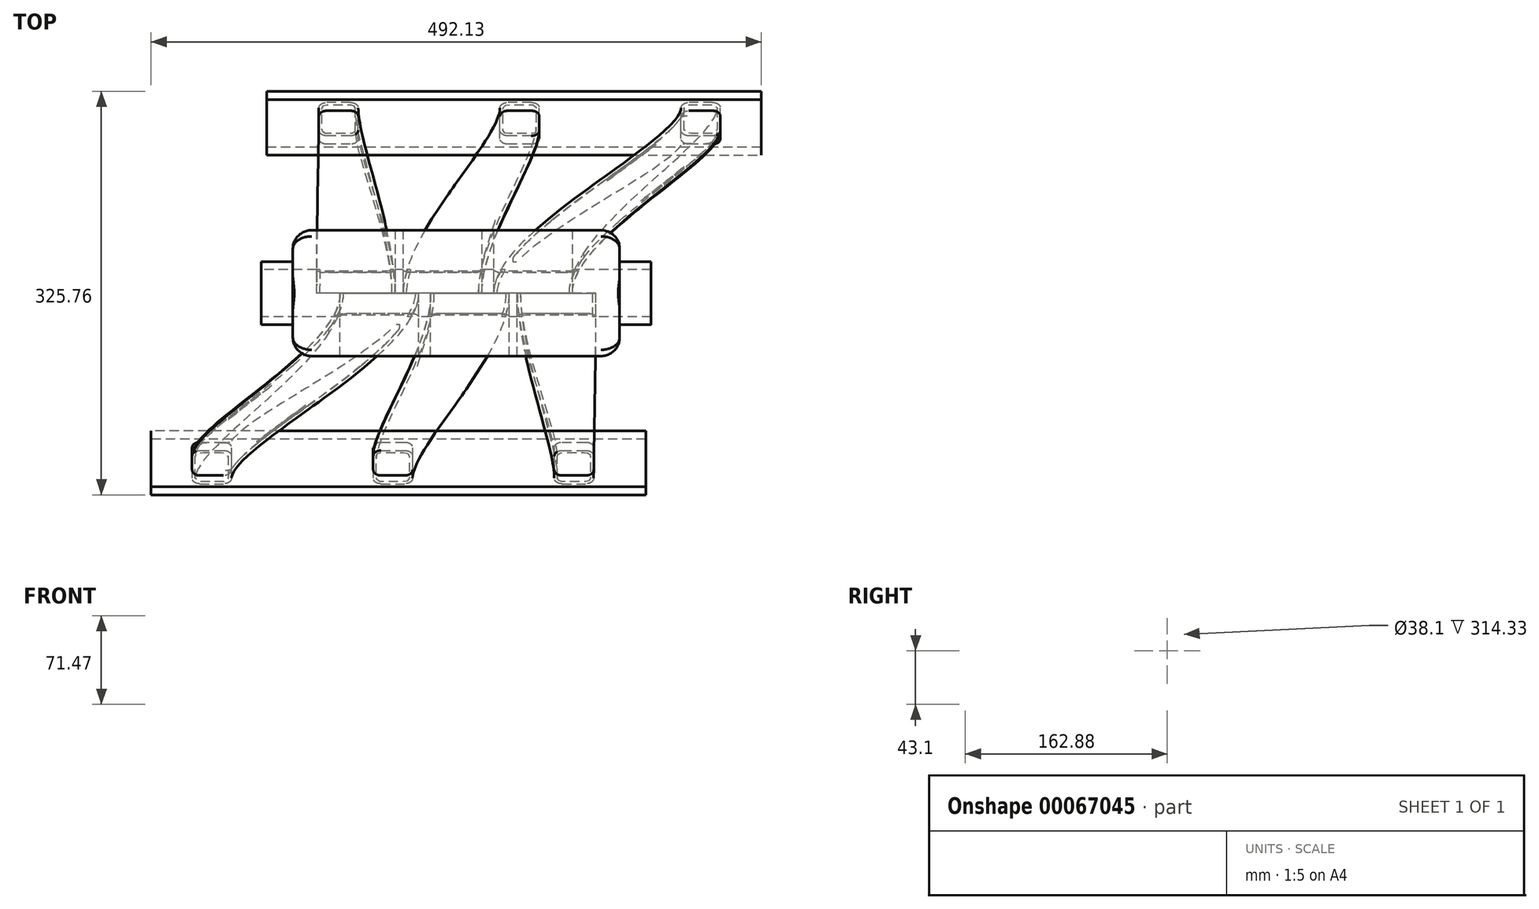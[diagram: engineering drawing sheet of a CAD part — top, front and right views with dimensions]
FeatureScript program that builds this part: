
annotation { "Feature Type Name" : "Feature", "Feature Type Description" : "" }
export const myFeature = defineFeature(function(context is Context, id is Id, definition is map)
    precondition{}
    {
        {
            var Q0;
            Q0=qCreatedBy(makeId("Front.planeOp"),FACE);
            var sketch = newSketch(context, id + "F0", { "sketchPlane" : qUnion([Q0])});
            skLineSegment(sketch, "E0.bottom", {"start": v(-123.83, 301.55) * mm, "end": v(139.7, 301.55) * mm});
            skLineSegment(sketch, "E0.top", {"start": v(-123.83, 230.08) * mm, "end": v(139.7, 230.08) * mm});
            skLineSegment(sketch, "E0.left", {"start": v(-123.83, 301.55) * mm, "end": v(-123.83, 230.08) * mm});
            skLineSegment(sketch, "E0.right", {"start": v(139.7, 301.55) * mm, "end": v(139.7, 230.08) * mm});
            skLineSegment(sketch, "E1.bottom", {"start": v(63.5, 282.5) * mm, "end": v(114.3, 282.5) * mm});
            skLineSegment(sketch, "E1.top", {"start": v(63.5, 244.4) * mm, "end": v(114.3, 244.4) * mm});
            skLineSegment(sketch, "E1.left", {"start": v(57.15, 276.15) * mm, "end": v(57.15, 250.75) * mm});
            skLineSegment(sketch, "E1.right", {"start": v(120.65, 276.15) * mm, "end": v(120.65, 250.75) * mm});
            skPoint(sketch, "E2.visualSharp", {"position": v(57.15, 282.5) * mm});
            skArc(sketch, "E2.filletArc", {"start": v(63.5, 282.5) * mm, "mid": v(59, 280.64) * mm, "end": v(57.15, 276.15) * mm});
            skPoint(sketch, "E3.visualSharp", {"position": v(120.65, 282.5) * mm});
            skArc(sketch, "E3.filletArc", {"start": v(120.65, 276.15) * mm, "mid": v(118.8, 280.64) * mm, "end": v(114.3, 282.5) * mm});
            skPoint(sketch, "E4.visualSharp", {"position": v(120.65, 244.4) * mm});
            skArc(sketch, "E4.filletArc", {"start": v(114.3, 244.4) * mm, "mid": v(118.8, 246.26) * mm, "end": v(120.65, 250.75) * mm});
            skPoint(sketch, "E5.visualSharp", {"position": v(57.15, 244.4) * mm});
            skArc(sketch, "E5.filletArc", {"start": v(57.15, 250.75) * mm, "mid": v(59, 246.26) * mm, "end": v(63.5, 244.4) * mm});
            skLineSegment(sketch, "E6.1.0.0", {"start": v(-6.35, 282.5) * mm, "end": v(44.45, 282.5) * mm});
            skArc(sketch, "E6.1.0.1", {"start": v(-6.35, 282.5) * mm, "mid": v(-10.84, 280.64) * mm, "end": v(-12.7, 276.15) * mm});
            skLineSegment(sketch, "E6.1.0.2", {"start": v(-12.7, 276.15) * mm, "end": v(-12.7, 250.75) * mm});
            skArc(sketch, "E6.1.0.3", {"start": v(-12.7, 250.75) * mm, "mid": v(-10.84, 246.26) * mm, "end": v(-6.35, 244.4) * mm});
            skLineSegment(sketch, "E6.1.0.4", {"start": v(-6.35, 244.4) * mm, "end": v(44.45, 244.4) * mm});
            skArc(sketch, "E6.1.0.5", {"start": v(44.45, 244.4) * mm, "mid": v(48.94, 246.26) * mm, "end": v(50.8, 250.75) * mm});
            skLineSegment(sketch, "E6.1.0.6", {"start": v(50.8, 276.15) * mm, "end": v(50.8, 250.75) * mm});
            skArc(sketch, "E6.1.0.7", {"start": v(50.8, 276.15) * mm, "mid": v(48.94, 280.64) * mm, "end": v(44.45, 282.5) * mm});
            skLineSegment(sketch, "E6.direction1", {"start": v(63.5, 282.5) * mm, "end": v(-6.35, 282.5) * mm, "construction": true});
            skLineSegment(sketch, "E7.1.0.0", {"start": v(-85.73, 276.15) * mm, "end": v(-85.73, 250.75) * mm});
            skLineSegment(sketch, "E7.1.0.1", {"start": v(-79.38, 282.5) * mm, "end": v(-28.58, 282.5) * mm});
            skArc(sketch, "E7.1.0.2", {"start": v(-79.38, 282.5) * mm, "mid": v(-83.87, 280.64) * mm, "end": v(-85.73, 276.15) * mm});
            skArc(sketch, "E7.1.0.3", {"start": v(-85.73, 250.75) * mm, "mid": v(-83.87, 246.26) * mm, "end": v(-79.38, 244.4) * mm});
            skLineSegment(sketch, "E7.1.0.4", {"start": v(-79.38, 244.4) * mm, "end": v(-28.58, 244.4) * mm});
            skArc(sketch, "E7.1.0.5", {"start": v(-28.58, 244.4) * mm, "mid": v(-24.09, 246.26) * mm, "end": v(-22.23, 250.75) * mm});
            skLineSegment(sketch, "E7.1.0.6", {"start": v(-22.23, 276.15) * mm, "end": v(-22.23, 250.75) * mm});
            skArc(sketch, "E7.1.0.7", {"start": v(-22.23, 276.15) * mm, "mid": v(-24.09, 280.64) * mm, "end": v(-28.58, 282.5) * mm});
            skLineSegment(sketch, "E7.direction1", {"start": v(57.15, 250.75) * mm, "end": v(-85.73, 250.75) * mm, "construction": true});
            skSolve(sketch);
        }
        {
            var Q0;
            Q0=qCreatedBy(makeId("Front.planeOp"),FACE);
            var Q1;
            Q1=qCreatedBy(makeId("Top.planeOp"),FACE);
            cPlane(context, id + "F1", {"entities" : qUnion([Q0, Q1]), "cplaneType" : CPlaneType.MID_PLANE, "offset" : 152.4 * mm, "width" : 152.4 * mm, "height" : 152.4 * mm});
        }
        {
            var Q0;
            Q0=qCreatedBy(id+"F1.planeOp",FACE);
            cPlane(context, id + "F2", {"entities" : qUnion([Q0]), "cplaneType" : CPlaneType.OFFSET, "offset" : 82.55 * mm, "oppositeDirection" : true, "width" : 152.4 * mm, "height" : 152.4 * mm});
        }
        {
            var Q0;
            Q0=qCreatedBy(id+"F2.planeOp",FACE);
            var sketch = newSketch(context, id + "F3", { "sketchPlane" : qUnion([Q0])});
            skLineSegment(sketch, "E8.bottom", {"start": v(160.76, 312.9) * mm, "end": v(-238.13, 312.9) * mm});
            skLineSegment(sketch, "E8.top", {"start": v(160.76, 249.4) * mm, "end": v(-238.13, 249.4) * mm});
            skLineSegment(sketch, "E8.left", {"start": v(160.76, 312.9) * mm, "end": v(160.76, 249.4) * mm});
            skLineSegment(sketch, "E8.right", {"start": v(-238.13, 312.9) * mm, "end": v(-238.13, 249.4) * mm});
            skLineSegment(sketch, "E9.rect.bottom", {"start": v(-198.76, 262.1) * mm, "end": v(-179.71, 262.1) * mm});
            skLineSegment(sketch, "E9.rect.top", {"start": v(-198.76, 300.2) * mm, "end": v(-179.71, 300.2) * mm});
            skLineSegment(sketch, "E9.rect.left", {"start": v(-205.11, 268.45) * mm, "end": v(-205.11, 293.85) * mm});
            skLineSegment(sketch, "E9.rect.right", {"start": v(-173.36, 268.45) * mm, "end": v(-173.36, 293.85) * mm});
            skPoint(sketch, "E9.rect.middle", {"position": v(-189.24, 281.15) * mm});
            skLineSegment(sketch, "E10", {"start": v(-238.13, 281.15) * mm, "end": v(160.76, 281.15) * mm, "construction": true});
            skPoint(sketch, "E11.visualSharp", {"position": v(-173.36, 300.2) * mm});
            skArc(sketch, "E11.filletArc", {"start": v(-173.36, 293.85) * mm, "mid": v(-175.22, 298.34) * mm, "end": v(-179.71, 300.2) * mm});
            skPoint(sketch, "E12.visualSharp", {"position": v(-205.11, 300.2) * mm});
            skArc(sketch, "E12.filletArc", {"start": v(-198.76, 300.2) * mm, "mid": v(-203.25, 298.34) * mm, "end": v(-205.11, 293.85) * mm});
            skPoint(sketch, "E13.visualSharp", {"position": v(-173.36, 262.1) * mm});
            skArc(sketch, "E13.filletArc", {"start": v(-179.71, 262.1) * mm, "mid": v(-175.22, 263.96) * mm, "end": v(-173.36, 268.45) * mm});
            skPoint(sketch, "E14.visualSharp", {"position": v(-205.11, 262.1) * mm});
            skArc(sketch, "E14.filletArc", {"start": v(-205.11, 268.45) * mm, "mid": v(-203.25, 263.96) * mm, "end": v(-198.76, 262.1) * mm});
            skLineSegment(sketch, "E15.1.0.0", {"start": v(-52.71, 262.1) * mm, "end": v(-33.66, 262.1) * mm});
            skArc(sketch, "E15.1.0.1", {"start": v(-33.66, 262.1) * mm, "mid": v(-29.17, 263.96) * mm, "end": v(-27.31, 268.45) * mm});
            skLineSegment(sketch, "E15.1.0.2", {"start": v(-27.31, 268.45) * mm, "end": v(-27.31, 293.85) * mm});
            skArc(sketch, "E15.1.0.3", {"start": v(-27.31, 293.85) * mm, "mid": v(-29.17, 298.34) * mm, "end": v(-33.66, 300.2) * mm});
            skLineSegment(sketch, "E15.1.0.4", {"start": v(-52.71, 300.2) * mm, "end": v(-33.66, 300.2) * mm});
            skArc(sketch, "E15.1.0.5", {"start": v(-52.71, 300.2) * mm, "mid": v(-57.2, 298.34) * mm, "end": v(-59.06, 293.85) * mm});
            skLineSegment(sketch, "E15.1.0.6", {"start": v(-59.06, 268.45) * mm, "end": v(-59.06, 293.85) * mm});
            skArc(sketch, "E15.1.0.7", {"start": v(-59.06, 268.45) * mm, "mid": v(-57.2, 263.96) * mm, "end": v(-52.71, 262.1) * mm});
            skLineSegment(sketch, "E15.2.0.0", {"start": v(93.34, 262.1) * mm, "end": v(112.39, 262.1) * mm});
            skArc(sketch, "E15.2.0.1", {"start": v(112.39, 262.1) * mm, "mid": v(116.88, 263.96) * mm, "end": v(118.74, 268.45) * mm});
            skLineSegment(sketch, "E15.2.0.2", {"start": v(118.74, 268.45) * mm, "end": v(118.74, 293.85) * mm});
            skArc(sketch, "E15.2.0.3", {"start": v(118.74, 293.85) * mm, "mid": v(116.88, 298.34) * mm, "end": v(112.39, 300.2) * mm});
            skLineSegment(sketch, "E15.2.0.4", {"start": v(93.34, 300.2) * mm, "end": v(112.39, 300.2) * mm});
            skArc(sketch, "E15.2.0.5", {"start": v(93.34, 300.2) * mm, "mid": v(88.85, 298.34) * mm, "end": v(86.99, 293.85) * mm});
            skLineSegment(sketch, "E15.2.0.6", {"start": v(86.99, 268.45) * mm, "end": v(86.99, 293.85) * mm});
            skArc(sketch, "E15.2.0.7", {"start": v(86.99, 268.45) * mm, "mid": v(88.85, 263.96) * mm, "end": v(93.34, 262.1) * mm});
            skLineSegment(sketch, "E15.direction1", {"start": v(-198.76, 262.1) * mm, "end": v(-52.71, 262.1) * mm, "construction": true});
            skSolve(sketch);
        }
        {
            var Q0;
            Q0=makeQuery(id+"F0.imprint","IMPRINT",FACE,{"disambiguationData":[TD([[makeQuery(id+"F0.imprint","IMPRINT",EDGE,{"derivedFrom":sQuery(id+"F0.wireOp",EDGE,"E7.1.0.0")}),1.0]])]});
            var Q1;
            Q1=makeQuery(id+"F3.imprint","IMPRINT",FACE,{"disambiguationData":[TD([[makeQuery(id+"F3.imprint","IMPRINT",EDGE,{"derivedFrom":sQuery(id+"F3.wireOp",EDGE,"E9.rect.bottom")}),1.0]])]});
            loft(context, id + "F4", {"startCondition" : LoftEndDerivativeType.NORMAL_TO_PROFILE, "startMagnitude" : 1, "endCondition" : LoftEndDerivativeType.NORMAL_TO_PROFILE, "endMagnitude" : 1, "sheetProfilesArray" : [{ "sheetProfileEntities" : qUnion([Q0]) }, { "sheetProfileEntities" : qUnion([Q1]) }]});
        }
        {
            var Q0;
            Q0=makeQuery(id+"F0.imprint","IMPRINT",FACE,{"disambiguationData":[TD([[makeQuery(id+"F0.imprint","IMPRINT",EDGE,{"derivedFrom":sQuery(id+"F0.wireOp",EDGE,"E6.1.0.0")}),-1.0]])]});
            var Q1;
            Q1=makeQuery(id+"F3.imprint","IMPRINT",FACE,{"disambiguationData":[TD([[makeQuery(id+"F3.imprint","IMPRINT",EDGE,{"derivedFrom":sQuery(id+"F3.wireOp",EDGE,"E15.1.0.0")}),1.0]])]});
            loft(context, id + "F5", {"startCondition" : LoftEndDerivativeType.NORMAL_TO_PROFILE, "startMagnitude" : 1, "endCondition" : LoftEndDerivativeType.NORMAL_TO_PROFILE, "endMagnitude" : 1, "sheetProfilesArray" : [{ "sheetProfileEntities" : qUnion([Q0]) }, { "sheetProfileEntities" : qUnion([Q1]) }]});
        }
        {
            var Q0;
            Q0=makeQuery(id+"F0.imprint","IMPRINT",FACE,{"disambiguationData":[TD([[makeQuery(id+"F0.imprint","IMPRINT",EDGE,{"derivedFrom":sQuery(id+"F0.wireOp",EDGE,"E1.bottom")}),-1.0]])]});
            var Q1;
            Q1=makeQuery(id+"F3.imprint","IMPRINT",FACE,{"disambiguationData":[TD([[makeQuery(id+"F3.imprint","IMPRINT",EDGE,{"derivedFrom":sQuery(id+"F3.wireOp",EDGE,"E15.2.0.0")}),1.0]])]});
            loft(context, id + "F6", {"startCondition" : LoftEndDerivativeType.NORMAL_TO_PROFILE, "startMagnitude" : 1, "endCondition" : LoftEndDerivativeType.NORMAL_TO_PROFILE, "endMagnitude" : 1, "sheetProfilesArray" : [{ "sheetProfileEntities" : qUnion([Q0]) }, { "sheetProfileEntities" : qUnion([Q1]) }]});
        }
        {
            var Q0;
            Q0=qSketchRegion(id+"F0",true);
            extrude(context, id + "F7", {"entities" : qUnion([Q0]), "depth" : 50.8 * mm});
        }
        {
            var Q0;
            Q0=makeQuery(id+"F4.opLoft","CAP_FACE",FACE,{"disambiguationData":[OSD([makeQuery(id+"F3.imprint","IMPRINT",FACE,{"disambiguationData":[TD([[makeQuery(id+"F3.imprint","IMPRINT",EDGE,{"derivedFrom":sQuery(id+"F3.wireOp",EDGE,"E9.rect.bottom")}),1.0]])]})])],"isStart":true});
            var Q1;
            Q1=makeQuery(id+"F4.opLoft","CAP_FACE",FACE,{"disambiguationData":[OSD([makeQuery(id+"F0.imprint","IMPRINT",FACE,{"disambiguationData":[TD([[makeQuery(id+"F0.imprint","IMPRINT",EDGE,{"derivedFrom":sQuery(id+"F0.wireOp",EDGE,"E7.1.0.0")}),1.0]])]})])],"isStart":true});
            shell(context, id + "F8", {"entities" : qUnion([Q0, Q1]), "thickness" : 2.54 * mm});
        }
        {
            var Q0;
            Q0=makeQuery(id+"F5.opLoft","CAP_FACE",FACE,{"disambiguationData":[OSD([makeQuery(id+"F0.imprint","IMPRINT",FACE,{"disambiguationData":[TD([[makeQuery(id+"F0.imprint","IMPRINT",EDGE,{"derivedFrom":sQuery(id+"F0.wireOp",EDGE,"E6.1.0.0")}),-1.0]])]})])],"isStart":true});
            var Q1;
            Q1=makeQuery(id+"F5.opLoft","CAP_FACE",FACE,{"disambiguationData":[OSD([makeQuery(id+"F3.imprint","IMPRINT",FACE,{"disambiguationData":[TD([[makeQuery(id+"F3.imprint","IMPRINT",EDGE,{"derivedFrom":sQuery(id+"F3.wireOp",EDGE,"E15.1.0.0")}),1.0]])]})])],"isStart":true});
            var Q2;
            Q2=makeQuery(id+"F5.opLoft","SWEPT_BODY",BODY,{"disambiguationData":[OSD([makeQuery(id+"F0.imprint","IMPRINT",FACE,{"disambiguationData":[TD([[makeQuery(id+"F0.imprint","IMPRINT",EDGE,{"derivedFrom":sQuery(id+"F0.wireOp",EDGE,"E6.1.0.0")}),-1.0]])]}),makeQuery(id+"F3.imprint","IMPRINT",FACE,{"disambiguationData":[TD([[makeQuery(id+"F3.imprint","IMPRINT",EDGE,{"derivedFrom":sQuery(id+"F3.wireOp",EDGE,"E15.1.0.0")}),1.0]])]})])]});
            shell(context, id + "F9", {"entities" : qUnion([Q0, Q1]), "parts" : qUnion([Q2]), "thickness" : 2.54 * mm});
        }
        {
            var Q0;
            Q0=makeQuery(id+"F6.opLoft","CAP_FACE",FACE,{"disambiguationData":[OSD([makeQuery(id+"F0.imprint","IMPRINT",FACE,{"disambiguationData":[TD([[makeQuery(id+"F0.imprint","IMPRINT",EDGE,{"derivedFrom":sQuery(id+"F0.wireOp",EDGE,"E1.bottom")}),-1.0]])]})])],"isStart":true});
            var Q1;
            Q1=makeQuery(id+"F6.opLoft","CAP_FACE",FACE,{"disambiguationData":[OSD([makeQuery(id+"F3.imprint","IMPRINT",FACE,{"disambiguationData":[TD([[makeQuery(id+"F3.imprint","IMPRINT",EDGE,{"derivedFrom":sQuery(id+"F3.wireOp",EDGE,"E15.2.0.0")}),1.0]])]})])],"isStart":true});
            shell(context, id + "F10", {"entities" : qUnion([Q0, Q1]), "thickness" : 2.54 * mm});
        }
        {
            var Q0;
            Q0=qSketchRegion(id+"F3",true);
            extrude(context, id + "F11", {"entities" : qUnion([Q0]), "oppositeDirection" : true, "depth" : 9.52 * mm});
        }
        {
            var Q0;
            Q0=makeQuery(id+"F7.opExtrude","CAP_EDGE",EDGE,{"disambiguationData":[OSD([sQuery(id+"F0.wireOp",EDGE,"E0.bottom")])],"isStart":false});
            fillet(context, id + "F12", {"entities" : qUnion([Q0]), "radius" : 5 * mm, "tangentPropagation" : true, "allowEdgeOverflow" : false});
        }
        {
            var Q0;
            Q0=makeQuery(id+"F7.opExtrude","SWEPT_EDGE",EDGE,{"disambiguationData":[OSD([sQuery(id+"F0.wireOp",EDGE,"E0.bottom"),sQuery(id+"F0.wireOp",EDGE,"E0.right")])]});
            fillet(context, id + "F13", {"entities" : qUnion([Q0]), "radius" : 15 * mm, "tangentPropagation" : true, "allowEdgeOverflow" : false});
        }
        {
            var Q0;
            Q0=makeQuery(id+"F7.opExtrude","SWEPT_EDGE",EDGE,{"disambiguationData":[OSD([sQuery(id+"F0.wireOp",EDGE,"E0.bottom"),sQuery(id+"F0.wireOp",EDGE,"E0.left")])]});
            fillet(context, id + "F14", {"entities" : qUnion([Q0]), "radius" : 15 * mm, "tangentPropagation" : true, "allowEdgeOverflow" : false});
        }
        {
            var Q0;
            Q0=makeQuery(id+"F7.opExtrude","CAP_FACE",FACE,{"disambiguationData":[OSD([sQuery(id+"F0.wireOp",EDGE,"E0.bottom"),sQuery(id+"F0.wireOp",EDGE,"E0.top"),sQuery(id+"F0.wireOp",EDGE,"E0.left"),sQuery(id+"F0.wireOp",EDGE,"E0.right"),sQuery(id+"F0.wireOp",EDGE,"E1.bottom"),sQuery(id+"F0.wireOp",EDGE,"E1.top"),sQuery(id+"F0.wireOp",EDGE,"E1.left"),sQuery(id+"F0.wireOp",EDGE,"E1.right"),sQuery(id+"F0.wireOp",EDGE,"E2.filletArc"),sQuery(id+"F0.wireOp",EDGE,"E3.filletArc"),sQuery(id+"F0.wireOp",EDGE,"E4.filletArc"),sQuery(id+"F0.wireOp",EDGE,"E5.filletArc"),sQuery(id+"F0.wireOp",EDGE,"E6.1.0.0"),sQuery(id+"F0.wireOp",EDGE,"E6.1.0.1"),sQuery(id+"F0.wireOp",EDGE,"E6.1.0.2"),sQuery(id+"F0.wireOp",EDGE,"E6.1.0.3"),sQuery(id+"F0.wireOp",EDGE,"E6.1.0.4"),sQuery(id+"F0.wireOp",EDGE,"E6.1.0.5"),sQuery(id+"F0.wireOp",EDGE,"E6.1.0.6"),sQuery(id+"F0.wireOp",EDGE,"E6.1.0.7"),sQuery(id+"F0.wireOp",EDGE,"E7.1.0.0"),sQuery(id+"F0.wireOp",EDGE,"E7.1.0.1"),sQuery(id+"F0.wireOp",EDGE,"E7.1.0.2"),sQuery(id+"F0.wireOp",EDGE,"E7.1.0.3"),sQuery(id+"F0.wireOp",EDGE,"E7.1.0.4"),sQuery(id+"F0.wireOp",EDGE,"E7.1.0.5"),sQuery(id+"F0.wireOp",EDGE,"E7.1.0.6"),sQuery(id+"F0.wireOp",EDGE,"E7.1.0.7")])],"isStart":true});
            var sketch = newSketch(context, id + "F15", { "sketchPlane" : qUnion([Q0])});
            skLineSegment(sketch, "E16", {"start": v(-7.93, 301.55) * mm, "end": v(-7.93, 230.08) * mm, "construction": true});
            skSolve(sketch);
        }
        {
            var Q0;
            Q0=makeQuery(id+"F11.opExtrude","SWEPT_BODY",BODY,{"disambiguationData":[OSD([sQuery(id+"F3.wireOp",EDGE,"E8.bottom"),sQuery(id+"F3.wireOp",EDGE,"E8.top"),sQuery(id+"F3.wireOp",EDGE,"E8.left"),sQuery(id+"F3.wireOp",EDGE,"E8.right"),sQuery(id+"F3.wireOp",EDGE,"E9.rect.bottom"),sQuery(id+"F3.wireOp",EDGE,"E9.rect.top"),sQuery(id+"F3.wireOp",EDGE,"E9.rect.left"),sQuery(id+"F3.wireOp",EDGE,"E9.rect.right"),sQuery(id+"F3.wireOp",EDGE,"E11.filletArc"),sQuery(id+"F3.wireOp",EDGE,"E12.filletArc"),sQuery(id+"F3.wireOp",EDGE,"E13.filletArc"),sQuery(id+"F3.wireOp",EDGE,"E14.filletArc"),sQuery(id+"F3.wireOp",EDGE,"E15.1.0.0"),sQuery(id+"F3.wireOp",EDGE,"E15.1.0.1"),sQuery(id+"F3.wireOp",EDGE,"E15.1.0.2"),sQuery(id+"F3.wireOp",EDGE,"E15.1.0.3"),sQuery(id+"F3.wireOp",EDGE,"E15.1.0.4"),sQuery(id+"F3.wireOp",EDGE,"E15.1.0.5"),sQuery(id+"F3.wireOp",EDGE,"E15.1.0.6"),sQuery(id+"F3.wireOp",EDGE,"E15.1.0.7"),sQuery(id+"F3.wireOp",EDGE,"E15.2.0.0"),sQuery(id+"F3.wireOp",EDGE,"E15.2.0.1"),sQuery(id+"F3.wireOp",EDGE,"E15.2.0.2"),sQuery(id+"F3.wireOp",EDGE,"E15.2.0.3"),sQuery(id+"F3.wireOp",EDGE,"E15.2.0.4"),sQuery(id+"F3.wireOp",EDGE,"E15.2.0.5"),sQuery(id+"F3.wireOp",EDGE,"E15.2.0.6"),sQuery(id+"F3.wireOp",EDGE,"E15.2.0.7")])]});
            var Q1;
            Q1=makeQuery(id+"F6.opLoft","SWEPT_BODY",BODY,{"disambiguationData":[OSD([makeQuery(id+"F0.imprint","IMPRINT",FACE,{"disambiguationData":[TD([[makeQuery(id+"F0.imprint","IMPRINT",EDGE,{"derivedFrom":sQuery(id+"F0.wireOp",EDGE,"E1.bottom")}),-1.0]])]}),makeQuery(id+"F3.imprint","IMPRINT",FACE,{"disambiguationData":[TD([[makeQuery(id+"F3.imprint","IMPRINT",EDGE,{"derivedFrom":sQuery(id+"F3.wireOp",EDGE,"E15.2.0.0")}),1.0]])]})])]});
            var Q2;
            Q2=makeQuery(id+"F5.opLoft","SWEPT_BODY",BODY,{"disambiguationData":[OSD([makeQuery(id+"F0.imprint","IMPRINT",FACE,{"disambiguationData":[TD([[makeQuery(id+"F0.imprint","IMPRINT",EDGE,{"derivedFrom":sQuery(id+"F0.wireOp",EDGE,"E6.1.0.0")}),-1.0]])]}),makeQuery(id+"F3.imprint","IMPRINT",FACE,{"disambiguationData":[TD([[makeQuery(id+"F3.imprint","IMPRINT",EDGE,{"derivedFrom":sQuery(id+"F3.wireOp",EDGE,"E15.1.0.0")}),1.0]])]})])]});
            var Q3;
            Q3=makeQuery(id+"F4.opLoft","SWEPT_BODY",BODY,{"disambiguationData":[OSD([makeQuery(id+"F0.imprint","IMPRINT",FACE,{"disambiguationData":[TD([[makeQuery(id+"F0.imprint","IMPRINT",EDGE,{"derivedFrom":sQuery(id+"F0.wireOp",EDGE,"E7.1.0.0")}),1.0]])]}),makeQuery(id+"F3.imprint","IMPRINT",FACE,{"disambiguationData":[TD([[makeQuery(id+"F3.imprint","IMPRINT",EDGE,{"derivedFrom":sQuery(id+"F3.wireOp",EDGE,"E9.rect.bottom")}),1.0]])]})])]});
            var Q4;
            Q4=makeQuery(id+"F7.opExtrude","SWEPT_BODY",BODY,{"disambiguationData":[OSD([sQuery(id+"F0.wireOp",EDGE,"E0.bottom"),sQuery(id+"F0.wireOp",EDGE,"E0.top"),sQuery(id+"F0.wireOp",EDGE,"E0.left"),sQuery(id+"F0.wireOp",EDGE,"E0.right"),sQuery(id+"F0.wireOp",EDGE,"E1.bottom"),sQuery(id+"F0.wireOp",EDGE,"E1.top"),sQuery(id+"F0.wireOp",EDGE,"E1.left"),sQuery(id+"F0.wireOp",EDGE,"E1.right"),sQuery(id+"F0.wireOp",EDGE,"E2.filletArc"),sQuery(id+"F0.wireOp",EDGE,"E3.filletArc"),sQuery(id+"F0.wireOp",EDGE,"E4.filletArc"),sQuery(id+"F0.wireOp",EDGE,"E5.filletArc"),sQuery(id+"F0.wireOp",EDGE,"E6.1.0.0"),sQuery(id+"F0.wireOp",EDGE,"E6.1.0.1"),sQuery(id+"F0.wireOp",EDGE,"E6.1.0.2"),sQuery(id+"F0.wireOp",EDGE,"E6.1.0.3"),sQuery(id+"F0.wireOp",EDGE,"E6.1.0.4"),sQuery(id+"F0.wireOp",EDGE,"E6.1.0.5"),sQuery(id+"F0.wireOp",EDGE,"E6.1.0.6"),sQuery(id+"F0.wireOp",EDGE,"E6.1.0.7"),sQuery(id+"F0.wireOp",EDGE,"E7.1.0.0"),sQuery(id+"F0.wireOp",EDGE,"E7.1.0.1"),sQuery(id+"F0.wireOp",EDGE,"E7.1.0.2"),sQuery(id+"F0.wireOp",EDGE,"E7.1.0.3"),sQuery(id+"F0.wireOp",EDGE,"E7.1.0.4"),sQuery(id+"F0.wireOp",EDGE,"E7.1.0.5"),sQuery(id+"F0.wireOp",EDGE,"E7.1.0.6"),sQuery(id+"F0.wireOp",EDGE,"E7.1.0.7")])]});
            var Q5;
            Q5=sQuery(id+"F15.wireOp",EDGE,"E16");
            circularPattern(context, id + "F16", {"entities" : qUnion([Q0, Q1, Q2, Q3, Q4]), "axis" : qUnion([Q5]), "angle" : 180 * degree, "instanceCount" : round(2), "equalSpace" : true});
        }
        {
            var Q0;
            Q0=makeQuery(id+"F16.opPattern","COPY",FACE,{"derivedFrom":makeQuery(id+"F7.opExtrude","SWEPT_FACE",FACE,{"disambiguationData":[OSD([sQuery(id+"F0.wireOp",EDGE,"E0.left")])]}),"instanceName":"1"});
            var sketch = newSketch(context, id + "F17", { "sketchPlane" : qUnion([Q0])});
            skCircle(sketch, "E17", {"center": v(0, 273.68) * mm, "radius": 25.4 * mm});
            skSolve(sketch);
        }
        {
            var Q0;
            Q0=makeQuery(id+"F7.opExtrude","SWEPT_FACE",FACE,{"disambiguationData":[OSD([sQuery(id+"F0.wireOp",EDGE,"E0.left")])]});
            var sketch = newSketch(context, id + "F18", { "sketchPlane" : qUnion([Q0])});
            skCircle(sketch, "E18", {"center": v(0, 273.18) * mm, "radius": 25.4 * mm});
            skSolve(sketch);
        }
        {
            var Q0;
            Q0=qSketchRegion(id+"F17",true);
            extrude(context, id + "F19", {"entities" : qUnion([Q0]), "operationType" : NewBodyOperationType.ADD, "depth" : 25.4 * mm});
        }
        {
            var Q0;
            Q0=qSketchRegion(id+"F18",true);
            extrude(context, id + "F20", {"entities" : qUnion([Q0]), "operationType" : NewBodyOperationType.ADD, "depth" : 25.4 * mm});
        }
        {
            var Q0;
            Q0=makeQuery(id+"F20.opExtrude","CAP_FACE",FACE,{"disambiguationData":[OSD([sQuery(id+"F18.wireOp",EDGE,"E18")])],"isStart":false});
            var sketch = newSketch(context, id + "F21", { "sketchPlane" : qUnion([Q0])});
            skCircle(sketch, "E19", {"center": v(0, 273.18) * mm, "radius": 19.05 * mm});
            skSolve(sketch);
        }
        {
            var Q0;
            Q0=makeQuery(id+"F21.imprint","IMPRINT",FACE,{"disambiguationData":[TD([[makeQuery(id+"F21.imprint","IMPRINT",EDGE,{"derivedFrom":sQuery(id+"F21.wireOp",EDGE,"E19")}),1.0]])]});
            extrude(context, id + "F22", {"entities" : qUnion([Q0]), "operationType" : NewBodyOperationType.REMOVE, "endBound" : BoundingType.THROUGH_ALL, "oppositeDirection" : true, "depth" : 25.4 * mm});
        }
    });
